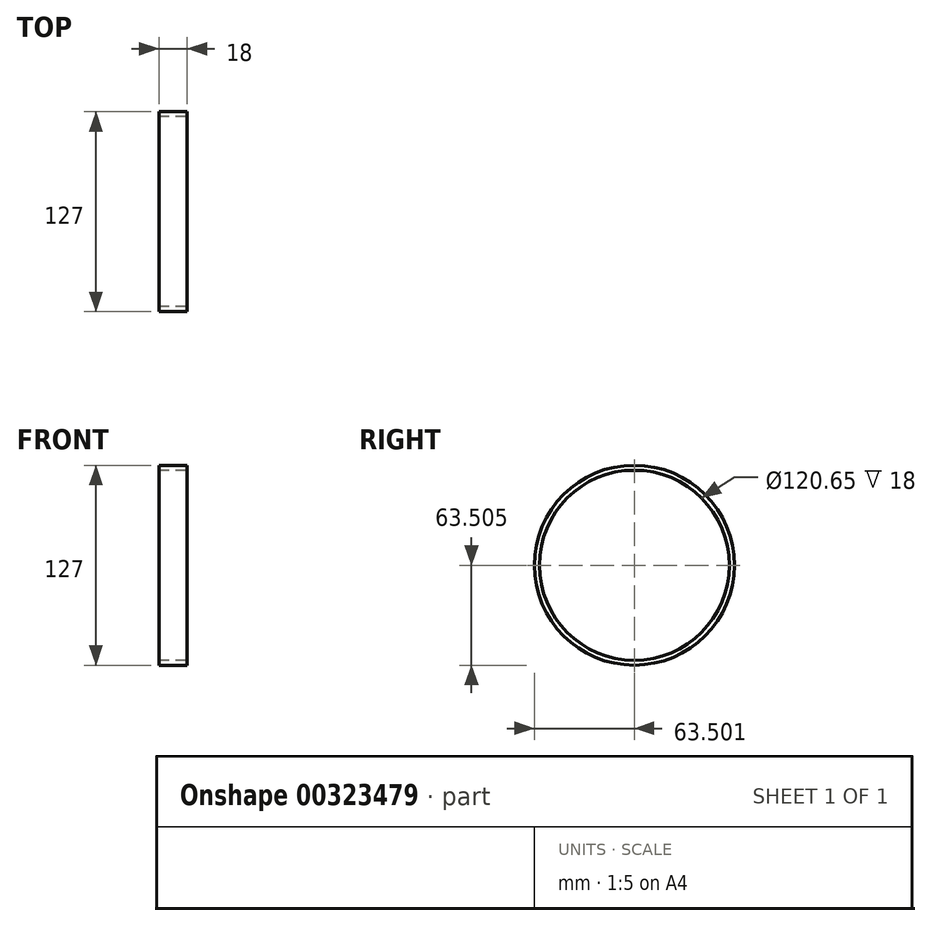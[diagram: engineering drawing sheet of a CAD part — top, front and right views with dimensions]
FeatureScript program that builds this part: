
annotation { "Feature Type Name" : "Feature", "Feature Type Description" : "" }
export const myFeature = defineFeature(function(context is Context, id is Id, definition is map)
    precondition{}
    {
        {
            assignVariable(context, id + "F0", {"name" : "length", "anyValue" : 18});
        }
        {
            var Q0;
            Q0=qCreatedBy(makeId("Right.planeOp"),FACE);
            var sketch = newSketch(context, id + "F1", { "sketchPlane" : qUnion([Q0])});
            skCircle(sketch, "E0", {"center": v(13.93, 20.1) * mm, "radius": 63.5 * mm});
            skCircle(sketch, "E1", {"center": v(13.93, 20.1) * mm, "radius": 60.33 * mm});
            skSolve(sketch);
        }
        {
            var Q0;
            Q0=makeQuery(id+"F1.imprint","IMPRINT",FACE,{"disambiguationData":[TD([[makeQuery(id+"F1.imprint","IMPRINT",EDGE,{"derivedFrom":sQuery(id+"F1.wireOp",EDGE,"E0")}),1.0]])]});
            extrude(context, id + "F2", {"entities" : qUnion([Q0]), "depth" : (getVariable(context, 'length')) * mm});
        }
    });
